# Revit family: Folha única
name_source: partatom
category: Portas
revit_build: Autodesk Revit Architecture 2015 (Build: 20140323_1530(x64)
units: mm (PartAtom-declared; Revit-internal decimal feet)

## types (7) — shared parameters
Coeficiente de transferência de calor (U) = 3.7021 W/(m²·K)
Construção analítica = Metal
Espessura = 51  [stored 0.167323 ft]
Fechamento da parede = Por hospedeiro
Função = Interior
ID do tipo de construção = MPORTA
Largura da apara = 76  [stored 0.249344 ft]
Material da estrutura = Porta - Batente
Material da porta = Porta - Painel
Projeção da apara externa = 25  [stored 0.082021 ft]
Projeção da apara interna = 25  [stored 0.082021 ft]
zero-valued in all types: Coeficiente de ganho de calor solar, Transmissão de luz visual

## per-type parameters (varying)
| type | Altura | Largura |
| 0915 x 2134mm | 2134  [stored 7.00131 ft] | 915  [stored 3.00197 ft] |
| 0864 x 2134mm | 2134  [stored 7.00131 ft] | 864 |
| 0813 x 2134mm | 2134  [stored 7.00131 ft] | 813  [stored 2.66732 ft] |
| 0762 x 2134mm | 2134  [stored 7.00131 ft] | 762 |
| 0762 x 2032mm | 2032  [stored 6.66667 ft] | 762 |
| 0915 x 2032mm | 2032  [stored 6.66667 ft] | 915  [stored 3.00197 ft] |
| 0864 x 2032mm | 2032  [stored 6.66667 ft] | 864 |

note: [stored X ft] marks values corroborated as IEEE doubles in the binary element streams (Revit-internal decimal feet)
